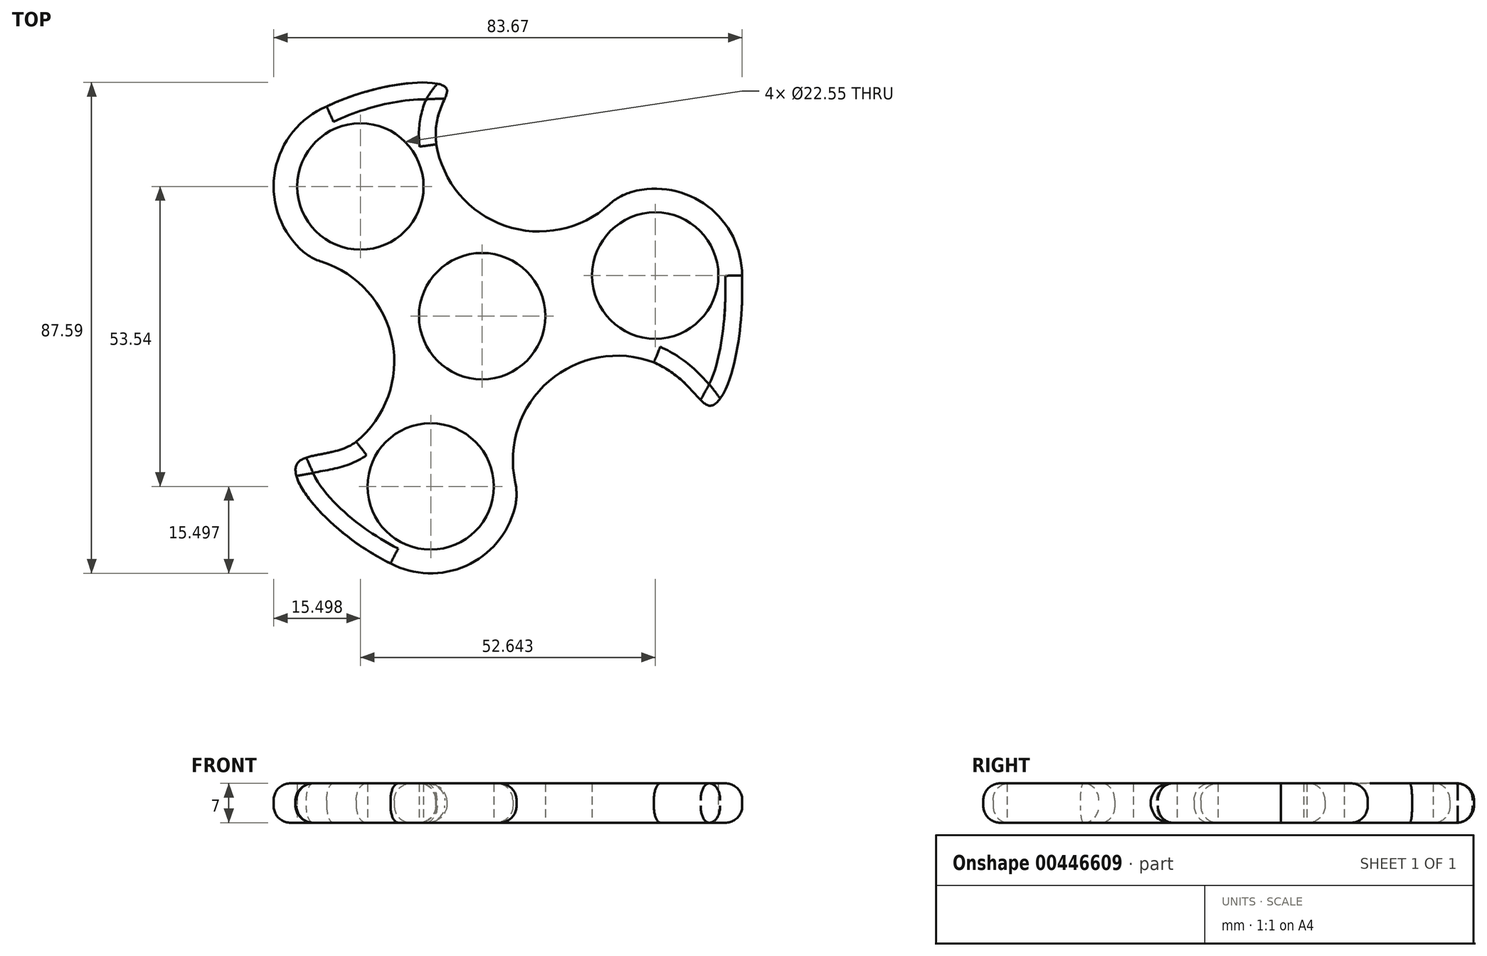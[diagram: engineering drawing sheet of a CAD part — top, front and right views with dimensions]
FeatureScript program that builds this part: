
annotation { "Feature Type Name" : "Feature", "Feature Type Description" : "" }
export const myFeature = defineFeature(function(context is Context, id is Id, definition is map)
    precondition{}
    {
        {
            var Q0;
            Q0=qCreatedBy(makeId("Top.planeOp"),FACE);
            var sketch = newSketch(context, id + "F0", { "sketchPlane" : qUnion([Q0])});
            skCircle(sketch, "E0", {"center": v(0, 0) * mm, "radius": 31.75 * mm});
            skCircle(sketch, "E1", {"center": v(30.91, 7.25) * mm, "radius": 15.5 * mm});
            skCircle(sketch, "E2", {"center": v(-21.73, 23.15) * mm, "radius": 15.5 * mm});
            skCircle(sketch, "E3", {"center": v(-9.18, -30.4) * mm, "radius": 15.5 * mm});
            skCircle(sketch, "E4", {"center": v(0, 0) * mm, "radius": 11.28 * mm});
            skCircle(sketch, "E5", {"center": v(30.91, 7.25) * mm, "radius": 11.28 * mm});
            skCircle(sketch, "E6", {"center": v(-21.73, 23.15) * mm, "radius": 11.28 * mm});
            skCircle(sketch, "E7", {"center": v(-9.18, -30.4) * mm, "radius": 11.28 * mm});
            skFitSpline(sketch, "E8", {"points": [v(46.41, 7.25) * mm, v(40.78, -15.98) * mm, v(30.66, -8.25) * mm], "startDerivative": vector(2, -70.39) * mm, "endDerivative": vector(-46.71, 20.98) * mm});
            skFitSpline(sketch, "E9", {"points": [v(-15.37, -44.6) * mm, v(-33.08, -26.4) * mm, v(-22.48, -22.42) * mm], "startDerivative": vector(-54.82, 25.3) * mm, "endDerivative": vector(26.74, 20.08) * mm});
            skFitSpline(sketch, "E10", {"points": [v(-29.73, 36.43) * mm, v(-6.45, 40.76) * mm, v(-8.18, 30.68) * mm], "startDerivative": vector(48.54, 26.45) * mm, "endDerivative": vector(5.73, -46.94) * mm});
            skArc(sketch, "E11", {"start": v(-8.18, 30.68) * mm, "mid": v(4.8, 15.9) * mm, "end": v(23.8, 21.02) * mm});
            skArc(sketch, "E12", {"start": v(30.66, -8.25) * mm, "mid": v(11.37, -12.1) * mm, "end": v(6.3, -31.12) * mm});
            skArc(sketch, "E13", {"start": v(-22.48, -22.42) * mm, "mid": v(-16.18, -3.8) * mm, "end": v(-30.1, 10.1) * mm});
            skSolve(sketch);
        }
        {
            var Q0;
            {var subQ0=sQuery(id+"F0.wireOp",EDGE,"E10");var subQ1=sQuery(id+"F0.wireOp",EDGE,"E2");var subQ2=makeQuery(id+"F0.imprint","INTERSECT",VERTEX,{"disambiguationData":[OD(0.0)],"derivedFrom":[subQ1,subQ0]});Q0=makeQuery(id+"F0.imprint","IMPRINT",FACE,{"disambiguationData":[TD([[makeQuery(id+"F0.imprint","IMPRINT",EDGE,{"disambiguationData":[TD([[subQ2,1.0]])],"derivedFrom":subQ1}),1.0]])]});}
            var Q1;
            {var subQ3=sQuery(id+"F0.wireOp",EDGE,"E0");var subQ7=sQuery(id+"F0.wireOp",EDGE,"E6");var subQ9=makeQuery(id+"F0.imprint","INTERSECT",VERTEX,{"disambiguationData":[OD(0.0)],"derivedFrom":[subQ3,subQ7]});Q1=makeQuery(id+"F0.imprint","IMPRINT",FACE,{"disambiguationData":[TD([[makeQuery(id+"F0.imprint","IMPRINT",EDGE,{"disambiguationData":[TD([[subQ9,-1.0]])],"derivedFrom":subQ7}),-1.0]])]});}
            var Q2;
            {var subQ0=sQuery(id+"F0.wireOp",EDGE,"E10");var subQ1=sQuery(id+"F0.wireOp",EDGE,"E2");var subQ3=makeQuery(id+"F0.imprint","INTERSECT",VERTEX,{"disambiguationData":[OD(1.0)],"derivedFrom":[subQ1,subQ0]});Q2=makeQuery(id+"F0.imprint","IMPRINT",FACE,{"disambiguationData":[TD([[makeQuery(id+"F0.imprint","IMPRINT",EDGE,{"disambiguationData":[TD([[subQ3,1.0]])],"derivedFrom":subQ1}),-1.0]])]});}
            var Q3;
            Q3=makeQuery(id+"F0.imprint","IMPRINT",FACE,{"disambiguationData":[TD([[makeQuery(id+"F0.imprint","IMPRINT",EDGE,{"derivedFrom":sQuery(id+"F0.wireOp",EDGE,"E4")}),-1.0]])]});
            var Q4;
            {var subQ0=sQuery(id+"F0.wireOp",EDGE,"E9");var subQ1=sQuery(id+"F0.wireOp",EDGE,"E3");var subQ2=makeQuery(id+"F0.imprint","INTERSECT",VERTEX,{"disambiguationData":[OD(0.0)],"derivedFrom":[subQ1,subQ0]});Q4=makeQuery(id+"F0.imprint","IMPRINT",FACE,{"disambiguationData":[TD([[makeQuery(id+"F0.imprint","IMPRINT",EDGE,{"disambiguationData":[TD([[subQ2,1.0]])],"derivedFrom":subQ1}),1.0]])]});}
            var Q5;
            {var subQ3=sQuery(id+"F0.wireOp",EDGE,"E0");var subQ7=sQuery(id+"F0.wireOp",EDGE,"E7");var subQ9=makeQuery(id+"F0.imprint","INTERSECT",VERTEX,{"disambiguationData":[OD(0.0)],"derivedFrom":[subQ3,subQ7]});Q5=makeQuery(id+"F0.imprint","IMPRINT",FACE,{"disambiguationData":[TD([[makeQuery(id+"F0.imprint","IMPRINT",EDGE,{"disambiguationData":[TD([[subQ9,-1.0]])],"derivedFrom":subQ7}),-1.0]])]});}
            var Q6;
            {var subQ0=sQuery(id+"F0.wireOp",EDGE,"E9");var subQ1=sQuery(id+"F0.wireOp",EDGE,"E3");var subQ3=makeQuery(id+"F0.imprint","INTERSECT",VERTEX,{"disambiguationData":[OD(1.0)],"derivedFrom":[subQ1,subQ0]});Q6=makeQuery(id+"F0.imprint","IMPRINT",FACE,{"disambiguationData":[TD([[makeQuery(id+"F0.imprint","IMPRINT",EDGE,{"disambiguationData":[TD([[subQ3,1.0]])],"derivedFrom":subQ1}),-1.0]])]});}
            var Q7;
            {var subQ0=sQuery(id+"F0.wireOp",EDGE,"E8");Q7=makeQuery(id+"F0.imprint","IMPRINT",FACE,{"disambiguationData":[TD([[makeQuery(id+"F0.imprint","IMPRINT",EDGE,{"derivedFrom":subQ0}),-1.0]])]});}
            var Q8;
            {var subQ3=sQuery(id+"F0.wireOp",EDGE,"E0");var subQ6=sQuery(id+"F0.wireOp",EDGE,"E5");var subQ8=makeQuery(id+"F0.imprint","INTERSECT",VERTEX,{"disambiguationData":[OD(0.0)],"derivedFrom":[subQ3,subQ6]});Q8=makeQuery(id+"F0.imprint","IMPRINT",FACE,{"disambiguationData":[TD([[makeQuery(id+"F0.imprint","IMPRINT",EDGE,{"disambiguationData":[TD([[subQ8,1.0]])],"derivedFrom":subQ6}),-1.0]])]});}
            var Q9;
            {var subQ4=sQuery(id+"F0.wireOp",EDGE,"E11");var subQ5=sQuery(id+"F0.wireOp",EDGE,"E2");var subQ6=makeQuery(id+"F0.imprint","INTERSECT",VERTEX,{"derivedFrom":[subQ5,subQ4]});Q9=makeQuery(id+"F0.imprint","IMPRINT",FACE,{"disambiguationData":[TD([[makeQuery(id+"F0.imprint","IMPRINT",EDGE,{"disambiguationData":[TD([[subQ6,1.0]])],"derivedFrom":subQ5}),1.0]])]});}
            var Q10;
            {var subQ0=sQuery(id+"F0.wireOp",EDGE,"E11");var subQ1=sQuery(id+"F0.wireOp",EDGE,"E1");var subQ2=makeQuery(id+"F0.imprint","INTERSECT",VERTEX,{"derivedFrom":[subQ1,subQ0]});Q10=makeQuery(id+"F0.imprint","IMPRINT",FACE,{"disambiguationData":[TD([[makeQuery(id+"F0.imprint","IMPRINT",EDGE,{"disambiguationData":[TD([[subQ2,-1.0]])],"derivedFrom":subQ1}),1.0]])]});}
            var Q11;
            {var subQ5=sQuery(id+"F0.wireOp",EDGE,"E3");var subQ8=sQuery(id+"F0.wireOp",EDGE,"E13");var subQ9=makeQuery(id+"F0.imprint","INTERSECT",VERTEX,{"derivedFrom":[subQ5,subQ8]});Q11=makeQuery(id+"F0.imprint","IMPRINT",FACE,{"disambiguationData":[TD([[makeQuery(id+"F0.imprint","IMPRINT",EDGE,{"disambiguationData":[TD([[subQ9,1.0]])],"derivedFrom":subQ5}),1.0]])]});}
            extrude(context, id + "F1", {"entities" : qUnion([Q0, Q1, Q2, Q3, Q4, Q5, Q6, Q7, Q8, Q9, Q10, Q11]), "depth" : 7 * mm});
        }
        {
            var Q0;
            Q0=makeQuery(id+"F1.opExtrude","SWEPT_EDGE",EDGE,{"disambiguationData":[OSD([sQuery(id+"F0.wireOp",EDGE,"E0"),sQuery(id+"F0.wireOp",EDGE,"E1"),sQuery(id+"F0.wireOp",EDGE,"E11")])]});
            var Q1;
            Q1=makeQuery(id+"F1.opExtrude","SWEPT_EDGE",EDGE,{"disambiguationData":[OSD([sQuery(id+"F0.wireOp",EDGE,"E0"),sQuery(id+"F0.wireOp",EDGE,"E3"),sQuery(id+"F0.wireOp",EDGE,"E12")])]});
            var Q2;
            Q2=makeQuery(id+"F1.opExtrude","SWEPT_EDGE",EDGE,{"disambiguationData":[OSD([sQuery(id+"F0.wireOp",EDGE,"E0"),sQuery(id+"F0.wireOp",EDGE,"E2"),sQuery(id+"F0.wireOp",EDGE,"E13")])]});
            fillet(context, id + "F2", {"entities" : qUnion([Q0, Q1, Q2]), "radius" : 10 * mm, "tangentPropagation" : true, "allowEdgeOverflow" : false});
        }
        {
            var Q0;
            Q0=makeQuery(id+"F1.opExtrude","CAP_EDGE",EDGE,{"disambiguationData":[OSD([sQuery(id+"F0.wireOp",EDGE,"E9")])],"isStart":false});
            var Q1;
            Q1=makeQuery(id+"F1.opExtrude","CAP_EDGE",EDGE,{"disambiguationData":[OSD([sQuery(id+"F0.wireOp",EDGE,"E13")])],"isStart":false});
            var Q2;
            Q2=makeQuery(id+"F1.opExtrude","CAP_EDGE",EDGE,{"disambiguationData":[OSD([sQuery(id+"F0.wireOp",EDGE,"E2")])],"isStart":false});
            var Q3;
            {var subQ0=sQuery(id+"F0.wireOp",EDGE,"E13");var subQ1=sQuery(id+"F0.wireOp",EDGE,"E2");Q3=makeQuery(id+"F2.opFillet","BLEND_EDGE",EDGE,{"blendedFrom":[makeQuery(id+"F1.opExtrude","SWEPT_EDGE",EDGE,{"disambiguationData":[OSD([sQuery(id+"F0.wireOp",EDGE,"E0"),subQ1,subQ0])]}),makeQuery(id+"F1.opExtrude","CAP_FACE",FACE,{"disambiguationData":[OSD([sQuery(id+"F0.wireOp",EDGE,"E1"),subQ1,sQuery(id+"F0.wireOp",EDGE,"E3"),sQuery(id+"F0.wireOp",EDGE,"E4"),sQuery(id+"F0.wireOp",EDGE,"E5"),sQuery(id+"F0.wireOp",EDGE,"E6"),sQuery(id+"F0.wireOp",EDGE,"E7"),sQuery(id+"F0.wireOp",EDGE,"E8"),sQuery(id+"F0.wireOp",EDGE,"E9"),sQuery(id+"F0.wireOp",EDGE,"E10"),sQuery(id+"F0.wireOp",EDGE,"E11"),sQuery(id+"F0.wireOp",EDGE,"E12"),subQ0])],"isStart":false})],"blendedInto":[makeQuery(id+"F1.opExtrude","CAP_FACE",FACE,{"disambiguationData":[OSD([sQuery(id+"F0.wireOp",EDGE,"E1"),subQ1,sQuery(id+"F0.wireOp",EDGE,"E3"),sQuery(id+"F0.wireOp",EDGE,"E4"),sQuery(id+"F0.wireOp",EDGE,"E5"),sQuery(id+"F0.wireOp",EDGE,"E6"),sQuery(id+"F0.wireOp",EDGE,"E7"),sQuery(id+"F0.wireOp",EDGE,"E8"),sQuery(id+"F0.wireOp",EDGE,"E9"),sQuery(id+"F0.wireOp",EDGE,"E10"),sQuery(id+"F0.wireOp",EDGE,"E11"),sQuery(id+"F0.wireOp",EDGE,"E12"),subQ0])],"isStart":false})]});}
            var Q4;
            Q4=makeQuery(id+"F1.opExtrude","CAP_EDGE",EDGE,{"disambiguationData":[OSD([sQuery(id+"F0.wireOp",EDGE,"E11")])],"isStart":false});
            var Q5;
            Q5=makeQuery(id+"F1.opExtrude","CAP_EDGE",EDGE,{"disambiguationData":[OSD([sQuery(id+"F0.wireOp",EDGE,"E10")])],"isStart":false});
            var Q6;
            {var subQ0=sQuery(id+"F0.wireOp",EDGE,"E11");var subQ1=sQuery(id+"F0.wireOp",EDGE,"E1");Q6=makeQuery(id+"F2.opFillet","BLEND_EDGE",EDGE,{"blendedFrom":[makeQuery(id+"F1.opExtrude","SWEPT_EDGE",EDGE,{"disambiguationData":[OSD([sQuery(id+"F0.wireOp",EDGE,"E0"),subQ1,subQ0])]}),makeQuery(id+"F1.opExtrude","CAP_FACE",FACE,{"disambiguationData":[OSD([subQ1,sQuery(id+"F0.wireOp",EDGE,"E2"),sQuery(id+"F0.wireOp",EDGE,"E3"),sQuery(id+"F0.wireOp",EDGE,"E4"),sQuery(id+"F0.wireOp",EDGE,"E5"),sQuery(id+"F0.wireOp",EDGE,"E6"),sQuery(id+"F0.wireOp",EDGE,"E7"),sQuery(id+"F0.wireOp",EDGE,"E8"),sQuery(id+"F0.wireOp",EDGE,"E9"),sQuery(id+"F0.wireOp",EDGE,"E10"),subQ0,sQuery(id+"F0.wireOp",EDGE,"E12"),sQuery(id+"F0.wireOp",EDGE,"E13")])],"isStart":false})],"blendedInto":[makeQuery(id+"F1.opExtrude","CAP_FACE",FACE,{"disambiguationData":[OSD([subQ1,sQuery(id+"F0.wireOp",EDGE,"E2"),sQuery(id+"F0.wireOp",EDGE,"E3"),sQuery(id+"F0.wireOp",EDGE,"E4"),sQuery(id+"F0.wireOp",EDGE,"E5"),sQuery(id+"F0.wireOp",EDGE,"E6"),sQuery(id+"F0.wireOp",EDGE,"E7"),sQuery(id+"F0.wireOp",EDGE,"E8"),sQuery(id+"F0.wireOp",EDGE,"E9"),sQuery(id+"F0.wireOp",EDGE,"E10"),subQ0,sQuery(id+"F0.wireOp",EDGE,"E12"),sQuery(id+"F0.wireOp",EDGE,"E13")])],"isStart":false})]});}
            var Q7;
            Q7=makeQuery(id+"F1.opExtrude","CAP_EDGE",EDGE,{"disambiguationData":[OSD([sQuery(id+"F0.wireOp",EDGE,"E1")])],"isStart":false});
            var Q8;
            Q8=makeQuery(id+"F1.opExtrude","CAP_EDGE",EDGE,{"disambiguationData":[OSD([sQuery(id+"F0.wireOp",EDGE,"E8")])],"isStart":false});
            var Q9;
            Q9=makeQuery(id+"F1.opExtrude","CAP_EDGE",EDGE,{"disambiguationData":[OSD([sQuery(id+"F0.wireOp",EDGE,"E12")])],"isStart":false});
            var Q10;
            Q10=makeQuery(id+"F1.opExtrude","CAP_EDGE",EDGE,{"disambiguationData":[OSD([sQuery(id+"F0.wireOp",EDGE,"E3")])],"isStart":false});
            var Q11;
            {var subQ0=sQuery(id+"F0.wireOp",EDGE,"E12");var subQ1=sQuery(id+"F0.wireOp",EDGE,"E3");Q11=makeQuery(id+"F2.opFillet","BLEND_EDGE",EDGE,{"blendedFrom":[makeQuery(id+"F1.opExtrude","SWEPT_EDGE",EDGE,{"disambiguationData":[OSD([sQuery(id+"F0.wireOp",EDGE,"E0"),subQ1,subQ0])]}),makeQuery(id+"F1.opExtrude","CAP_FACE",FACE,{"disambiguationData":[OSD([sQuery(id+"F0.wireOp",EDGE,"E1"),sQuery(id+"F0.wireOp",EDGE,"E2"),subQ1,sQuery(id+"F0.wireOp",EDGE,"E4"),sQuery(id+"F0.wireOp",EDGE,"E5"),sQuery(id+"F0.wireOp",EDGE,"E6"),sQuery(id+"F0.wireOp",EDGE,"E7"),sQuery(id+"F0.wireOp",EDGE,"E8"),sQuery(id+"F0.wireOp",EDGE,"E9"),sQuery(id+"F0.wireOp",EDGE,"E10"),sQuery(id+"F0.wireOp",EDGE,"E11"),subQ0,sQuery(id+"F0.wireOp",EDGE,"E13")])],"isStart":false})],"blendedInto":[makeQuery(id+"F1.opExtrude","CAP_FACE",FACE,{"disambiguationData":[OSD([sQuery(id+"F0.wireOp",EDGE,"E1"),sQuery(id+"F0.wireOp",EDGE,"E2"),subQ1,sQuery(id+"F0.wireOp",EDGE,"E4"),sQuery(id+"F0.wireOp",EDGE,"E5"),sQuery(id+"F0.wireOp",EDGE,"E6"),sQuery(id+"F0.wireOp",EDGE,"E7"),sQuery(id+"F0.wireOp",EDGE,"E8"),sQuery(id+"F0.wireOp",EDGE,"E9"),sQuery(id+"F0.wireOp",EDGE,"E10"),sQuery(id+"F0.wireOp",EDGE,"E11"),subQ0,sQuery(id+"F0.wireOp",EDGE,"E13")])],"isStart":false})]});}
            fillet(context, id + "F3", {"entities" : qUnion([Q0, Q1, Q2, Q3, Q4, Q5, Q6, Q7, Q8, Q9, Q10, Q11]), "radius" : 3 * mm, "tangentPropagation" : true, "allowEdgeOverflow" : false});
        }
        {
            var Q0;
            Q0=makeQuery(id+"F1.opExtrude","CAP_EDGE",EDGE,{"disambiguationData":[OSD([sQuery(id+"F0.wireOp",EDGE,"E13")])],"isStart":true});
            var Q1;
            {var subQ0=sQuery(id+"F0.wireOp",EDGE,"E13");var subQ1=sQuery(id+"F0.wireOp",EDGE,"E2");Q1=makeQuery(id+"F2.opFillet","BLEND_EDGE",EDGE,{"blendedFrom":[makeQuery(id+"F1.opExtrude","SWEPT_EDGE",EDGE,{"disambiguationData":[OSD([sQuery(id+"F0.wireOp",EDGE,"E0"),subQ1,subQ0])]}),makeQuery(id+"F1.opExtrude","CAP_FACE",FACE,{"disambiguationData":[OSD([sQuery(id+"F0.wireOp",EDGE,"E1"),subQ1,sQuery(id+"F0.wireOp",EDGE,"E3"),sQuery(id+"F0.wireOp",EDGE,"E4"),sQuery(id+"F0.wireOp",EDGE,"E5"),sQuery(id+"F0.wireOp",EDGE,"E6"),sQuery(id+"F0.wireOp",EDGE,"E7"),sQuery(id+"F0.wireOp",EDGE,"E8"),sQuery(id+"F0.wireOp",EDGE,"E9"),sQuery(id+"F0.wireOp",EDGE,"E10"),sQuery(id+"F0.wireOp",EDGE,"E11"),sQuery(id+"F0.wireOp",EDGE,"E12"),subQ0])],"isStart":true})],"blendedInto":[makeQuery(id+"F1.opExtrude","CAP_FACE",FACE,{"disambiguationData":[OSD([sQuery(id+"F0.wireOp",EDGE,"E1"),subQ1,sQuery(id+"F0.wireOp",EDGE,"E3"),sQuery(id+"F0.wireOp",EDGE,"E4"),sQuery(id+"F0.wireOp",EDGE,"E5"),sQuery(id+"F0.wireOp",EDGE,"E6"),sQuery(id+"F0.wireOp",EDGE,"E7"),sQuery(id+"F0.wireOp",EDGE,"E8"),sQuery(id+"F0.wireOp",EDGE,"E9"),sQuery(id+"F0.wireOp",EDGE,"E10"),sQuery(id+"F0.wireOp",EDGE,"E11"),sQuery(id+"F0.wireOp",EDGE,"E12"),subQ0])],"isStart":true})]});}
            var Q2;
            Q2=makeQuery(id+"F1.opExtrude","CAP_EDGE",EDGE,{"disambiguationData":[OSD([sQuery(id+"F0.wireOp",EDGE,"E2")])],"isStart":true});
            var Q3;
            Q3=makeQuery(id+"F1.opExtrude","CAP_EDGE",EDGE,{"disambiguationData":[OSD([sQuery(id+"F0.wireOp",EDGE,"E10")])],"isStart":true});
            var Q4;
            Q4=makeQuery(id+"F1.opExtrude","CAP_EDGE",EDGE,{"disambiguationData":[OSD([sQuery(id+"F0.wireOp",EDGE,"E11")])],"isStart":true});
            var Q5;
            Q5=makeQuery(id+"F1.opExtrude","CAP_EDGE",EDGE,{"disambiguationData":[OSD([sQuery(id+"F0.wireOp",EDGE,"E1")])],"isStart":true});
            var Q6;
            {var subQ0=sQuery(id+"F0.wireOp",EDGE,"E11");var subQ1=sQuery(id+"F0.wireOp",EDGE,"E1");Q6=makeQuery(id+"F2.opFillet","BLEND_EDGE",EDGE,{"blendedFrom":[makeQuery(id+"F1.opExtrude","SWEPT_EDGE",EDGE,{"disambiguationData":[OSD([sQuery(id+"F0.wireOp",EDGE,"E0"),subQ1,subQ0])]}),makeQuery(id+"F1.opExtrude","CAP_FACE",FACE,{"disambiguationData":[OSD([subQ1,sQuery(id+"F0.wireOp",EDGE,"E2"),sQuery(id+"F0.wireOp",EDGE,"E3"),sQuery(id+"F0.wireOp",EDGE,"E4"),sQuery(id+"F0.wireOp",EDGE,"E5"),sQuery(id+"F0.wireOp",EDGE,"E6"),sQuery(id+"F0.wireOp",EDGE,"E7"),sQuery(id+"F0.wireOp",EDGE,"E8"),sQuery(id+"F0.wireOp",EDGE,"E9"),sQuery(id+"F0.wireOp",EDGE,"E10"),subQ0,sQuery(id+"F0.wireOp",EDGE,"E12"),sQuery(id+"F0.wireOp",EDGE,"E13")])],"isStart":true})],"blendedInto":[makeQuery(id+"F1.opExtrude","CAP_FACE",FACE,{"disambiguationData":[OSD([subQ1,sQuery(id+"F0.wireOp",EDGE,"E2"),sQuery(id+"F0.wireOp",EDGE,"E3"),sQuery(id+"F0.wireOp",EDGE,"E4"),sQuery(id+"F0.wireOp",EDGE,"E5"),sQuery(id+"F0.wireOp",EDGE,"E6"),sQuery(id+"F0.wireOp",EDGE,"E7"),sQuery(id+"F0.wireOp",EDGE,"E8"),sQuery(id+"F0.wireOp",EDGE,"E9"),sQuery(id+"F0.wireOp",EDGE,"E10"),subQ0,sQuery(id+"F0.wireOp",EDGE,"E12"),sQuery(id+"F0.wireOp",EDGE,"E13")])],"isStart":true})]});}
            var Q7;
            Q7=makeQuery(id+"F1.opExtrude","CAP_EDGE",EDGE,{"disambiguationData":[OSD([sQuery(id+"F0.wireOp",EDGE,"E8")])],"isStart":true});
            var Q8;
            Q8=makeQuery(id+"F1.opExtrude","CAP_EDGE",EDGE,{"disambiguationData":[OSD([sQuery(id+"F0.wireOp",EDGE,"E12")])],"isStart":true});
            var Q9;
            Q9=makeQuery(id+"F1.opExtrude","CAP_EDGE",EDGE,{"disambiguationData":[OSD([sQuery(id+"F0.wireOp",EDGE,"E3")])],"isStart":true});
            var Q10;
            {var subQ0=sQuery(id+"F0.wireOp",EDGE,"E12");var subQ1=sQuery(id+"F0.wireOp",EDGE,"E3");Q10=makeQuery(id+"F2.opFillet","BLEND_EDGE",EDGE,{"blendedFrom":[makeQuery(id+"F1.opExtrude","SWEPT_EDGE",EDGE,{"disambiguationData":[OSD([sQuery(id+"F0.wireOp",EDGE,"E0"),subQ1,subQ0])]}),makeQuery(id+"F1.opExtrude","CAP_FACE",FACE,{"disambiguationData":[OSD([sQuery(id+"F0.wireOp",EDGE,"E1"),sQuery(id+"F0.wireOp",EDGE,"E2"),subQ1,sQuery(id+"F0.wireOp",EDGE,"E4"),sQuery(id+"F0.wireOp",EDGE,"E5"),sQuery(id+"F0.wireOp",EDGE,"E6"),sQuery(id+"F0.wireOp",EDGE,"E7"),sQuery(id+"F0.wireOp",EDGE,"E8"),sQuery(id+"F0.wireOp",EDGE,"E9"),sQuery(id+"F0.wireOp",EDGE,"E10"),sQuery(id+"F0.wireOp",EDGE,"E11"),subQ0,sQuery(id+"F0.wireOp",EDGE,"E13")])],"isStart":true})],"blendedInto":[makeQuery(id+"F1.opExtrude","CAP_FACE",FACE,{"disambiguationData":[OSD([sQuery(id+"F0.wireOp",EDGE,"E1"),sQuery(id+"F0.wireOp",EDGE,"E2"),subQ1,sQuery(id+"F0.wireOp",EDGE,"E4"),sQuery(id+"F0.wireOp",EDGE,"E5"),sQuery(id+"F0.wireOp",EDGE,"E6"),sQuery(id+"F0.wireOp",EDGE,"E7"),sQuery(id+"F0.wireOp",EDGE,"E8"),sQuery(id+"F0.wireOp",EDGE,"E9"),sQuery(id+"F0.wireOp",EDGE,"E10"),sQuery(id+"F0.wireOp",EDGE,"E11"),subQ0,sQuery(id+"F0.wireOp",EDGE,"E13")])],"isStart":true})]});}
            var Q11;
            Q11=makeQuery(id+"F1.opExtrude","CAP_EDGE",EDGE,{"disambiguationData":[OSD([sQuery(id+"F0.wireOp",EDGE,"E9")])],"isStart":true});
            fillet(context, id + "F4", {"entities" : qUnion([Q0, Q1, Q2, Q3, Q4, Q5, Q6, Q7, Q8, Q9, Q10, Q11]), "radius" : 3 * mm, "tangentPropagation" : true, "allowEdgeOverflow" : false});
        }
    });
